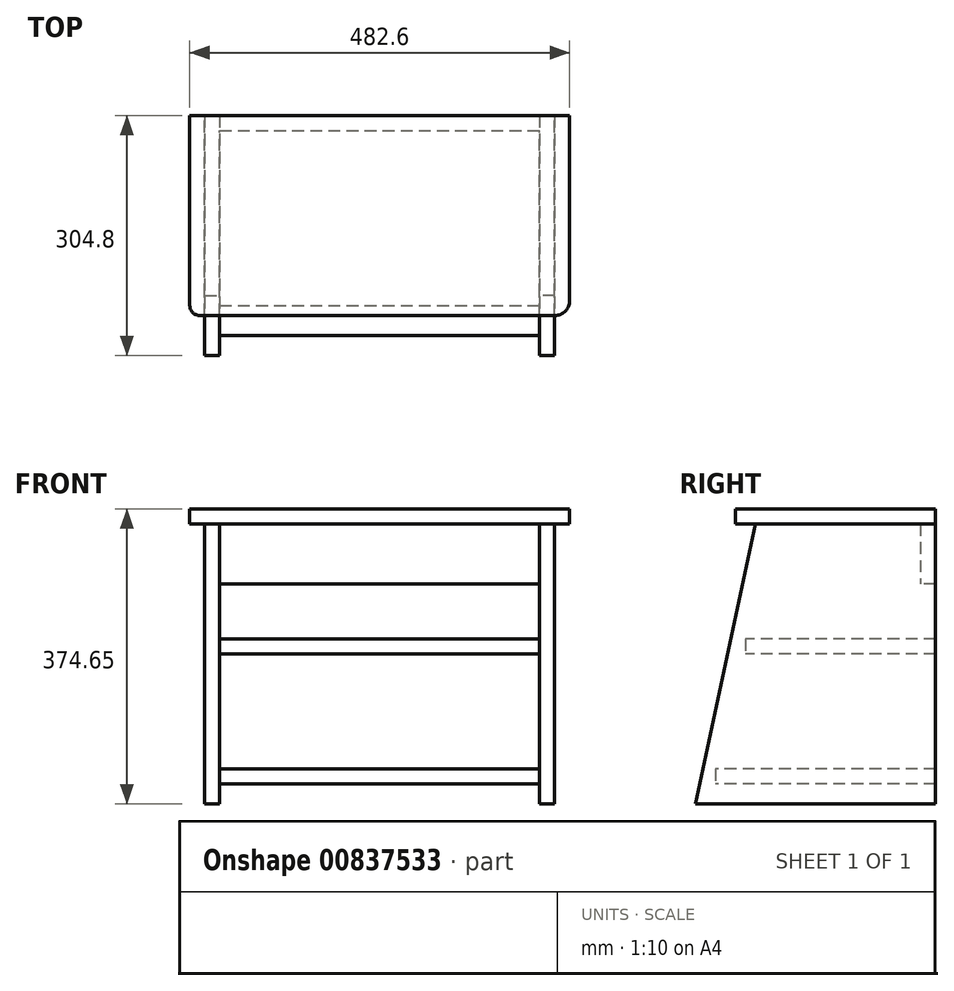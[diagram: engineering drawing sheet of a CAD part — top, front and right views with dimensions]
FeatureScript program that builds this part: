
annotation { "Feature Type Name" : "Feature", "Feature Type Description" : "" }
export const myFeature = defineFeature(function(context is Context, id is Id, definition is map)
    precondition{}
    {
        {
            var Q0;
            Q0=qCreatedBy(makeId("Right.planeOp"),FACE);
            var sketch = newSketch(context, id + "F0", { "sketchPlane" : qUnion([Q0])});
            skLineSegment(sketch, "E0", {"start": v(0, 0) * mm, "end": v(76.2, 355.6) * mm});
            skLineSegment(sketch, "E1", {"start": v(76.2, 355.6) * mm, "end": v(304.8, 355.6) * mm});
            skLineSegment(sketch, "E2", {"start": v(304.8, 355.6) * mm, "end": v(304.8, 0) * mm});
            skLineSegment(sketch, "E3", {"start": v(304.8, 0) * mm, "end": v(0, 0) * mm});
            skSolve(sketch);
        }
        {
            var Q0;
            Q0 = qSketchRegion(id + "F0", true);
            extrude(context, id + "F1", {"entities" : qUnion([Q0]), "depth" : 19.05 * mm, "offsetDistance" : 25.4 * mm});
        }
        {
            var Q0;
            Q0=makeQuery(id+"F1.opExtrude","CAP_FACE",FACE,{"disambiguationData":[OSD([sQuery(id+"F0.wireOp",EDGE,"E0"),sQuery(id+"F0.wireOp",EDGE,"E1"),sQuery(id+"F0.wireOp",EDGE,"E2"),sQuery(id+"F0.wireOp",EDGE,"E3")])],"isStart":true});
            var sketch = newSketch(context, id + "F2", { "sketchPlane" : qUnion([Q0])});
            skLineSegment(sketch, "E4.bottom", {"start": v(-304.8, 44.45) * mm, "end": v(-25.4, 44.45) * mm});
            skLineSegment(sketch, "E4.top", {"start": v(-304.8, 25.4) * mm, "end": v(-25.4, 25.4) * mm});
            skLineSegment(sketch, "E4.left", {"start": v(-304.8, 44.45) * mm, "end": v(-304.8, 25.4) * mm});
            skLineSegment(sketch, "E4.right", {"start": v(-25.4, 44.45) * mm, "end": v(-25.4, 25.4) * mm});
            skLineSegment(sketch, "E5.bottom", {"start": v(-304.8, 209.55) * mm, "end": v(-63.5, 209.55) * mm});
            skLineSegment(sketch, "E5.top", {"start": v(-304.8, 190.5) * mm, "end": v(-63.5, 190.5) * mm});
            skLineSegment(sketch, "E5.left", {"start": v(-304.8, 209.55) * mm, "end": v(-304.8, 190.5) * mm});
            skLineSegment(sketch, "E5.right", {"start": v(-63.5, 209.55) * mm, "end": v(-63.5, 190.5) * mm});
            skLineSegment(sketch, "E6.bottom", {"start": v(-304.8, 355.6) * mm, "end": v(-285.75, 355.6) * mm});
            skLineSegment(sketch, "E6.top", {"start": v(-304.8, 279.4) * mm, "end": v(-285.75, 279.4) * mm});
            skLineSegment(sketch, "E6.left", {"start": v(-304.8, 355.6) * mm, "end": v(-304.8, 279.4) * mm});
            skLineSegment(sketch, "E6.right", {"start": v(-285.75, 355.6) * mm, "end": v(-285.75, 279.4) * mm});
            skSolve(sketch);
        }
        {
            var Q0;
            Q0 = qSketchRegion(id + "F2", true);
            extrude(context, id + "F3", {"entities" : qUnion([Q0]), "operationType" : NewBodyOperationType.ADD, "depth" : 406.4 * mm, "offsetDistance" : 25.4 * mm});
        }
        {
            var Q0;
            Q0=makeQuery(id+"F3.opExtrude","CAP_FACE",FACE,{"disambiguationData":[OSD([sQuery(id+"F2.wireOp",EDGE,"E5.bottom"),sQuery(id+"F2.wireOp",EDGE,"E5.top"),sQuery(id+"F2.wireOp",EDGE,"E5.left"),sQuery(id+"F2.wireOp",EDGE,"E5.right")])],"isStart":false});
            var sketch = newSketch(context, id + "F4", { "sketchPlane" : qUnion([Q0])});
            skLineSegment(sketch, "E7.0", {"start": v(0, 0) * mm, "end": v(-76.2, 355.6) * mm});
            skLineSegment(sketch, "E7.1", {"start": v(-76.2, 355.6) * mm, "end": v(-304.8, 355.6) * mm});
            skLineSegment(sketch, "E7.2", {"start": v(-304.8, 355.6) * mm, "end": v(-304.8, 0) * mm});
            skLineSegment(sketch, "E7.3", {"start": v(-304.8, 0) * mm, "end": v(0, 0) * mm});
            skSolve(sketch);
        }
        {
            var Q0;
            Q0 = qSketchRegion(id + "F4", true);
            extrude(context, id + "F5", {"entities" : qUnion([Q0]), "operationType" : NewBodyOperationType.ADD, "depth" : 19.05 * mm, "offsetDistance" : 25.4 * mm});
        }
        {
            var Q0;
            Q0=makeQuery(id+"F5.boolean.opBoolean","MERGE",FACE,{"derivedFrom":[makeQuery(id+"F3.boolean.opBoolean","MERGE",FACE,{"derivedFrom":[makeQuery(id+"F1.opExtrude","SWEPT_FACE",FACE,{"disambiguationData":[OSD([sQuery(id+"F0.wireOp",EDGE,"E1")])]}),makeQuery(id+"F3.opExtrude","SWEPT_FACE",FACE,{"disambiguationData":[OSD([sQuery(id+"F2.wireOp",EDGE,"E6.bottom")])]})]}),makeQuery(id+"F5.opExtrude","SWEPT_FACE",FACE,{"disambiguationData":[OSD([sQuery(id+"F4.wireOp",EDGE,"E7.1")])]})]});
            var sketch = newSketch(context, id + "F6", { "sketchPlane" : qUnion([Q0])});
            skLineSegment(sketch, "E8.bottom", {"start": v(38.1, 304.8) * mm, "end": v(-444.5, 304.8) * mm});
            skLineSegment(sketch, "E8.top", {"start": v(19.05, 50.8) * mm, "end": v(-431.8, 50.8) * mm});
            skLineSegment(sketch, "E8.left", {"start": v(38.1, 304.8) * mm, "end": v(38.1, 69.85) * mm});
            skLineSegment(sketch, "E8.right", {"start": v(-444.5, 304.8) * mm, "end": v(-444.5, 63.5) * mm});
            skPoint(sketch, "E9.visualSharp", {"position": v(-444.5, 50.8) * mm});
            skArc(sketch, "E9.filletArc", {"start": v(-444.5, 63.5) * mm, "mid": v(-440.78, 54.52) * mm, "end": v(-431.8, 50.8) * mm});
            skPoint(sketch, "E10.visualSharp", {"position": v(38.1, 50.8) * mm});
            skArc(sketch, "E10.filletArc", {"start": v(19.05, 50.8) * mm, "mid": v(32.52, 56.38) * mm, "end": v(38.1, 69.85) * mm});
            skSolve(sketch);
        }
        {
            var Q0;
            Q0 = qSketchRegion(id + "F6", true);
            extrude(context, id + "F7", {"entities" : qUnion([Q0]), "operationType" : NewBodyOperationType.ADD, "depth" : 19.05 * mm, "offsetDistance" : 25.4 * mm});
        }
    });
